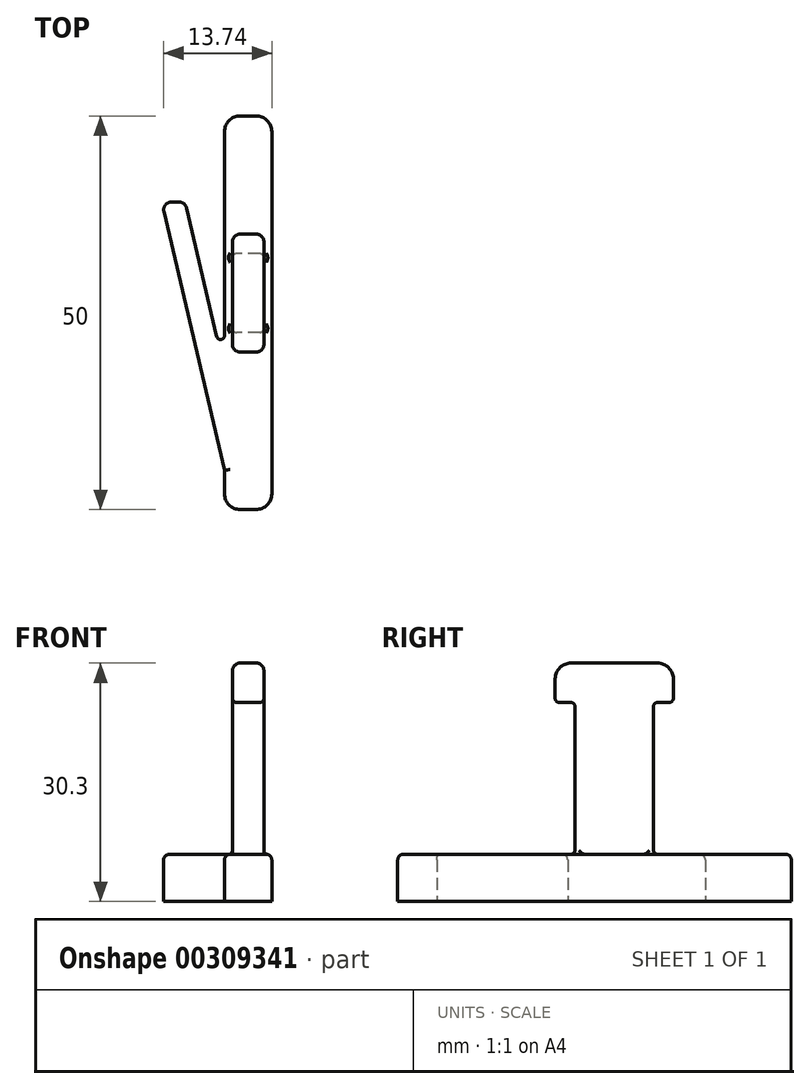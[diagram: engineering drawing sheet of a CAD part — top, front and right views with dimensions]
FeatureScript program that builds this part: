
annotation { "Feature Type Name" : "Feature", "Feature Type Description" : "" }
export const myFeature = defineFeature(function(context is Context, id is Id, definition is map)
    precondition{}
    {
        {
            var Q0;
            Q0=qCreatedBy(makeId("Top.planeOp"),FACE);
            var sketch = newSketch(context, id + "F0", { "sketchPlane" : qUnion([Q0])});
            skLineSegment(sketch, "E0.bottom", {"start": v(0, 0) * mm, "end": v(6, 0) * mm});
            skLineSegment(sketch, "E0.top", {"start": v(0, -50) * mm, "end": v(6, -50) * mm});
            skLineSegment(sketch, "E0.left", {"start": v(0, 0) * mm, "end": v(0, -50) * mm});
            skLineSegment(sketch, "E0.right", {"start": v(6, 0) * mm, "end": v(6, -50) * mm});
            skLineSegment(sketch, "E1", {"start": v(0, -50) * mm, "end": v(0, -45) * mm});
            skLineSegment(sketch, "E2", {"start": v(0, -45) * mm, "end": v(-8, -45) * mm});
            skLineSegment(sketch, "E3", {"start": v(0, -45) * mm, "end": v(-8, -10.93) * mm});
            skLineSegment(sketch, "E4", {"start": v(-8, -10.93) * mm, "end": v(-5, -10.93) * mm});
            skLineSegment(sketch, "E5", {"start": v(-5, -10.93) * mm, "end": v(0, -32.22) * mm});
            skSolve(sketch);
        }
        {
            var Q0;
            Q0=qSketchRegion(id+"F0",true);
            extrude(context, id + "F1", {"entities" : qUnion([Q0]), "depth" : 6 * mm});
        }
        {
            var Q0;
            Q0=makeQuery(id+"F1.opExtrude","SWEPT_EDGE",EDGE,{"disambiguationData":[OSD([sQuery(id+"F0.wireOp",EDGE,"E3"),sQuery(id+"F0.wireOp",EDGE,"E4")])]});
            var Q1;
            Q1=makeQuery(id+"F1.opExtrude","SWEPT_EDGE",EDGE,{"disambiguationData":[OSD([sQuery(id+"F0.wireOp",EDGE,"E4"),sQuery(id+"F0.wireOp",EDGE,"E5")])]});
            fillet(context, id + "F2", {"entities" : qUnion([Q0, Q1]), "radius" : 1 * mm, "tangentPropagation" : true, "allowEdgeOverflow" : false});
        }
        {
            var Q0;
            Q0=makeQuery(id+"F1.opExtrude","SWEPT_EDGE",EDGE,{"disambiguationData":[OSD([sQuery(id+"F0.wireOp",EDGE,"E0.left"),sQuery(id+"F0.wireOp",EDGE,"E5")])]});
            fillet(context, id + "F3", {"entities" : qUnion([Q0]), "radius" : .5 * mm, "tangentPropagation" : true, "allowEdgeOverflow" : false});
        }
        {
            var Q0;
            Q0=makeQuery(id+"F1.opExtrude","SWEPT_EDGE",EDGE,{"disambiguationData":[OSD([sQuery(id+"F0.wireOp",EDGE,"E0.bottom"),sQuery(id+"F0.wireOp",EDGE,"E0.left")])]});
            var Q1;
            Q1=makeQuery(id+"F1.opExtrude","SWEPT_EDGE",EDGE,{"disambiguationData":[OSD([sQuery(id+"F0.wireOp",EDGE,"E0.bottom"),sQuery(id+"F0.wireOp",EDGE,"E0.right")])]});
            var Q2;
            Q2=makeQuery(id+"F1.opExtrude","SWEPT_EDGE",EDGE,{"disambiguationData":[OSD([sQuery(id+"F0.wireOp",EDGE,"E0.top"),sQuery(id+"F0.wireOp",EDGE,"E0.right")])]});
            var Q3;
            Q3=makeQuery(id+"F1.opExtrude","SWEPT_EDGE",EDGE,{"disambiguationData":[OSD([sQuery(id+"F0.wireOp",EDGE,"E0.top"),sQuery(id+"F0.wireOp",EDGE,"E1")])]});
            fillet(context, id + "F4", {"entities" : qUnion([Q0, Q1, Q2, Q3]), "radius" : 2 * mm, "tangentPropagation" : true, "allowEdgeOverflow" : false});
        }
        {
            var Q0;
            Q0=makeQuery(id+"F1.opExtrude","CAP_FACE",FACE,{"disambiguationData":[OSD([sQuery(id+"F0.wireOp",EDGE,"E0.bottom"),sQuery(id+"F0.wireOp",EDGE,"E0.top"),sQuery(id+"F0.wireOp",EDGE,"E0.left"),sQuery(id+"F0.wireOp",EDGE,"E0.right"),sQuery(id+"F0.wireOp",EDGE,"E1"),sQuery(id+"F0.wireOp",EDGE,"E3"),sQuery(id+"F0.wireOp",EDGE,"E4"),sQuery(id+"F0.wireOp",EDGE,"E5")])],"isStart":false});
            fillet(context, id + "F5", {"entities" : qUnion([Q0]), "radius" : .7 * mm, "allowEdgeOverflow" : false});
        }
        {
            var Q0;
            Q0=makeQuery(id+"F1.opExtrude","SWEPT_FACE",FACE,{"disambiguationData":[OSD([sQuery(id+"F0.wireOp",EDGE,"E0.right")])]});
            var sketch = newSketch(context, id + "F6", { "sketchPlane" : qUnion([Q0])});
            skLineSegment(sketch, "E6.bottom", {"start": v(-27.5, 5.3) * mm, "end": v(-17.5, 5.3) * mm});
            skLineSegment(sketch, "E6.top", {"start": v(-27.5, 25.3) * mm, "end": v(-17.5, 25.3) * mm});
            skLineSegment(sketch, "E6.left", {"start": v(-27.5, 5.3) * mm, "end": v(-27.5, 25.3) * mm});
            skLineSegment(sketch, "E6.right", {"start": v(-17.5, 5.3) * mm, "end": v(-17.5, 25.3) * mm});
            skLineSegment(sketch, "E7.bottom", {"start": v(-30, 25.3) * mm, "end": v(-15, 25.3) * mm});
            skLineSegment(sketch, "E7.top", {"start": v(-30, 30.3) * mm, "end": v(-15, 30.3) * mm});
            skLineSegment(sketch, "E7.left", {"start": v(-30, 25.3) * mm, "end": v(-30, 30.3) * mm});
            skLineSegment(sketch, "E7.right", {"start": v(-15, 25.3) * mm, "end": v(-15, 30.3) * mm});
            skSolve(sketch);
        }
        {
            var Q0;
            Q0 = qSketchRegion(id + "F6", true);
            extrude(context, id + "F7", {"entities" : qUnion([Q0]), "operationType" : NewBodyOperationType.ADD, "oppositeDirection" : true, "depth" : 5 * mm, "hasSecondDirection" : true, "secondDirectionOppositeDirection" : true, "secondDirectionDepth" : 1 * mm});
        }
        {
            var Q0;
            Q0=makeQuery(id+"F7.opExtrude","SWEPT_FACE",FACE,{"disambiguationData":[OSD([sQuery(id+"F6.wireOp",EDGE,"E6.left")])]});
            var Q1;
            Q1=makeQuery(id+"F7.opExtrude","SWEPT_FACE",FACE,{"disambiguationData":[OSD([sQuery(id+"F6.wireOp",EDGE,"E6.right")])]});
            var Q2;
            {var subQ0=sQuery(id+"F6.wireOp",EDGE,"E7.bottom");Q2=makeQuery(id+"F7.opExtrude","SWEPT_FACE",FACE,{"disambiguationData":[OSD([subQ0]),TDD([makeQuery(id+"F6.imprint","IMPRINT",EDGE,{"disambiguationData":[TD([[makeQuery(id+"F6.imprint","INTERSECT",VERTEX,{"derivedFrom":[sQuery(id+"F6.wireOp",EDGE,"E6.left"),subQ0]}),1.0]])],"derivedFrom":subQ0})])]});}
            var Q3;
            {var subQ0=sQuery(id+"F6.wireOp",EDGE,"E7.bottom");Q3=makeQuery(id+"F7.opExtrude","SWEPT_FACE",FACE,{"disambiguationData":[OSD([subQ0]),TDD([makeQuery(id+"F6.imprint","IMPRINT",EDGE,{"disambiguationData":[TD([[makeQuery(id+"F6.imprint","INTERSECT",VERTEX,{"derivedFrom":[sQuery(id+"F6.wireOp",EDGE,"E6.right"),subQ0]}),-1.0]])],"derivedFrom":subQ0})])]});}
            fillet(context, id + "F8", {"entities" : qUnion([Q0, Q1, Q2, Q3]), "radius" : .5 * mm, "allowEdgeOverflow" : false});
        }
        {
            var Q0;
            Q0=makeQuery(id+"F7.opExtrude","SWEPT_EDGE",EDGE,{"disambiguationData":[OSD([sQuery(id+"F6.wireOp",EDGE,"E7.top"),sQuery(id+"F6.wireOp",EDGE,"E7.left")])]});
            var Q1;
            Q1=makeQuery(id+"F7.opExtrude","SWEPT_EDGE",EDGE,{"disambiguationData":[OSD([sQuery(id+"F6.wireOp",EDGE,"E7.top"),sQuery(id+"F6.wireOp",EDGE,"E7.right")])]});
            fillet(context, id + "F9", {"entities" : qUnion([Q0, Q1]), "radius" : 2 * mm, "tangentPropagation" : true, "allowEdgeOverflow" : false});
        }
        {
            var Q0;
            Q0=makeQuery(id+"F7.opExtrude","CAP_EDGE",EDGE,{"disambiguationData":[OSD([sQuery(id+"F6.wireOp",EDGE,"E7.left")])],"isStart":true});
            var Q1;
            Q1=makeQuery(id+"F7.opExtrude","CAP_EDGE",EDGE,{"disambiguationData":[OSD([sQuery(id+"F6.wireOp",EDGE,"E7.top")])],"isStart":true});
            var Q2;
            Q2=makeQuery(id+"F7.opExtrude","CAP_EDGE",EDGE,{"disambiguationData":[OSD([sQuery(id+"F6.wireOp",EDGE,"E7.right")])],"isStart":true});
            var Q3;
            Q3=makeQuery(id+"F7.opExtrude","CAP_EDGE",EDGE,{"disambiguationData":[OSD([sQuery(id+"F6.wireOp",EDGE,"E7.right")])],"isStart":false});
            fillet(context, id + "F10", {"entities" : qUnion([Q0, Q1, Q2, Q3]), "radius" : 1 * mm, "tangentPropagation" : true, "allowEdgeOverflow" : false});
        }
    });
